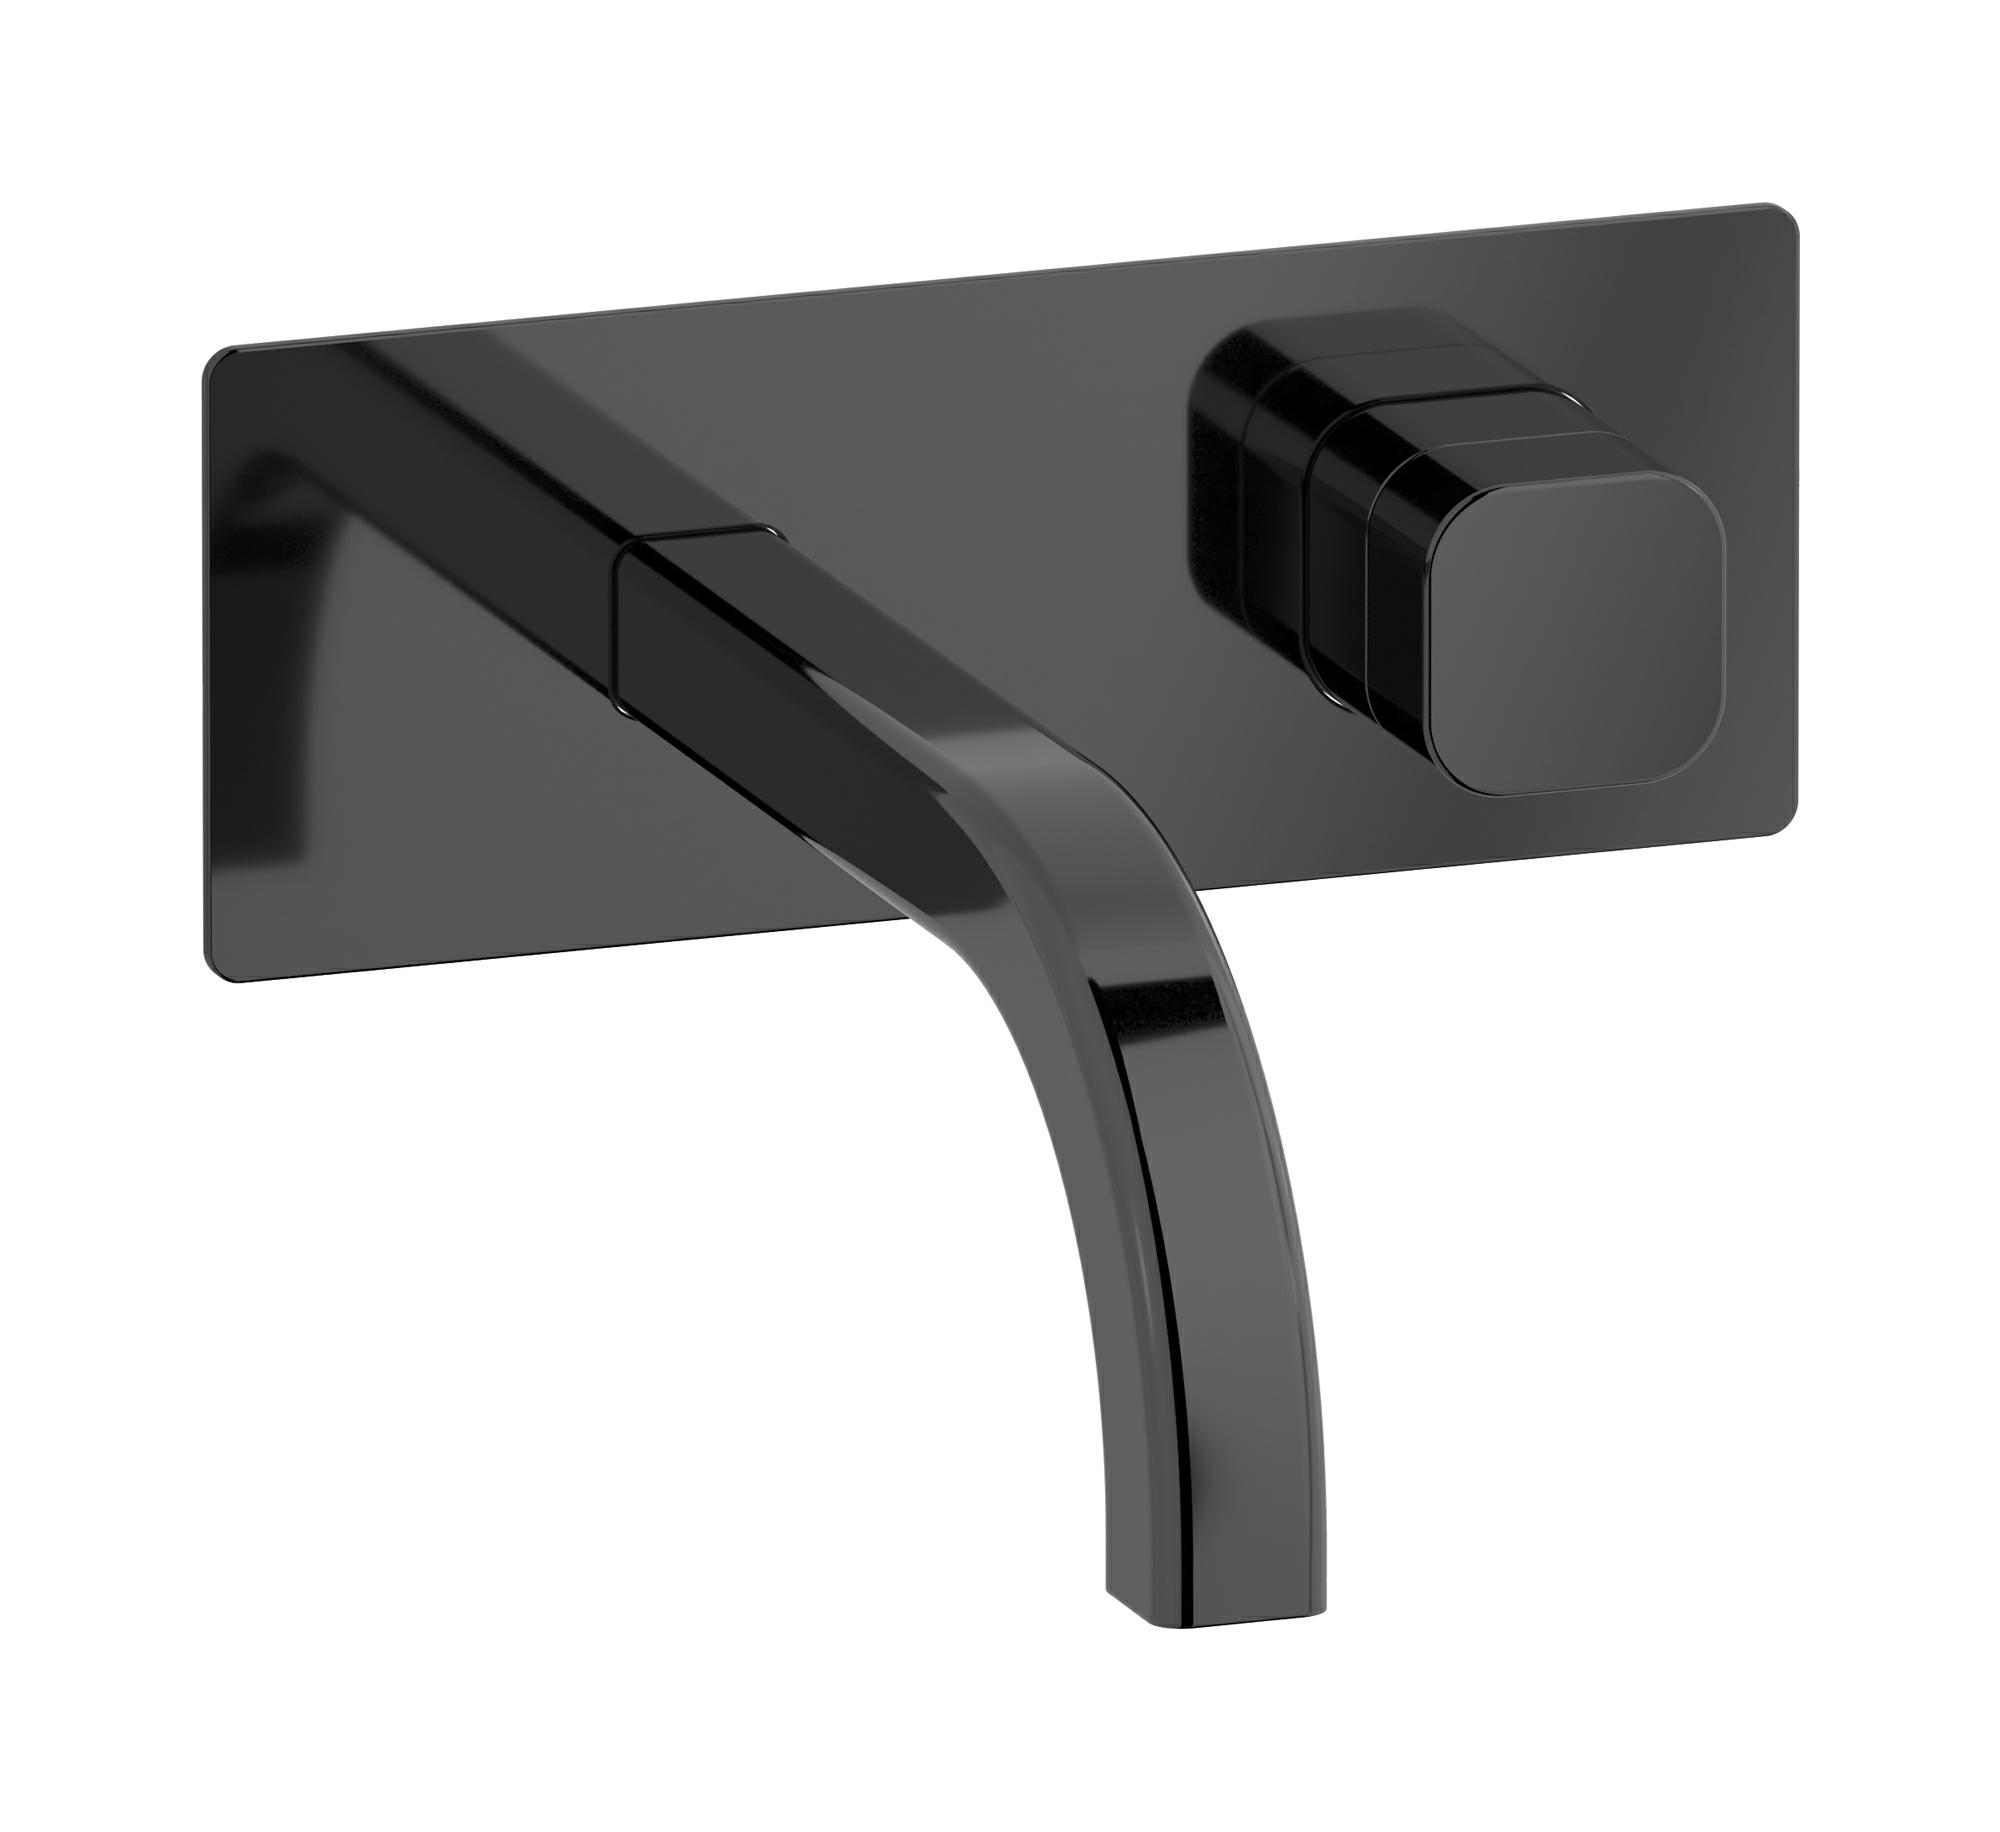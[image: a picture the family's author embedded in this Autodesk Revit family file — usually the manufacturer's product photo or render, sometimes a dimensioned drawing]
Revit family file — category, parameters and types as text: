
# Revit family: EO206_3
name_source: partatom
category: Apparecchi idraulici
units: mm (PartAtom-declared; Revit-internal decimal feet)

## family parameters
Basato su piano di lavoro = No
Condiviso = No
Mantieni orientamento annotazione = No
Numero OmniClass = 23.45.55.17
Punto di calcolo locali = No
Quota connettore circolare = Usa diametro
Sempre verticale = Sì
Taglio con vuoti quando caricato = No
Tipo di parte = Normale
Titolo OmniClass = Mixing Faucets

## types (12) — shared parameters
Cold water inlet = -10 mm  [stored -0.0328084 ft]
Commenti sul tipo = Washbasin
Connessione CW = No
Connessione HW = No
Connessione di scarico = No
Connessione di ventilazione = No
Descrizione = Wall mounted washbasin
Hot water inlet = 10 mm  [stored 0.0328084 ft]
Produttore = IB Rubinetterie S.p.A.
URL = https://www.weareib.it
zero-valued in all types: Prospetto di default

## per-type parameters (varying)
| type | Finishes surface | Immagine tipo | Modello |
| Chrome | IB_Chrome | EO206CC_3.jpg | EO206CC_3 |
| Brushed nickel | IB_Brushed nickel | EO206SS_3.jpg | EO206SS_3 |
| Natural Brass | IB_Brass | EO206ON_3.jpg | EO206ON_3 |
| Black chrome | IB_Black chrome | EO206CF_3.jpg | EO206CF_3 |
| Matt black | IB_matt black | EO206NP_3.jpg | EO206NP_3 |
| Brushed black chrome | IB_Brushed black chrome | EO206CS_3.jpg | EO206CS_3 |
| Pale gold | IB_Pale gold | EO206II_3.jpg | EO206II_3 |
| Brushed pale gold | IB_brushed pale gold | EO206IS_3.jpg | EO206IS_3 |
| Rose gold | IB_Rose gold | EO206RS_3.jpg | EO206RS_3 |
| Brushed rose gold | IB_Brushed rose gold | EO206SR_3.jpg | EO206SR_3 |
| Gold | IB_gold | EO206OO_3.jpg | EO206OO_3 |
| Brushed gold | IB_brushed gold | EO206OS_3.jpg | EO206OS_3 |

note: [stored X ft] marks values corroborated as IEEE doubles in the binary element streams (Revit-internal decimal feet)
